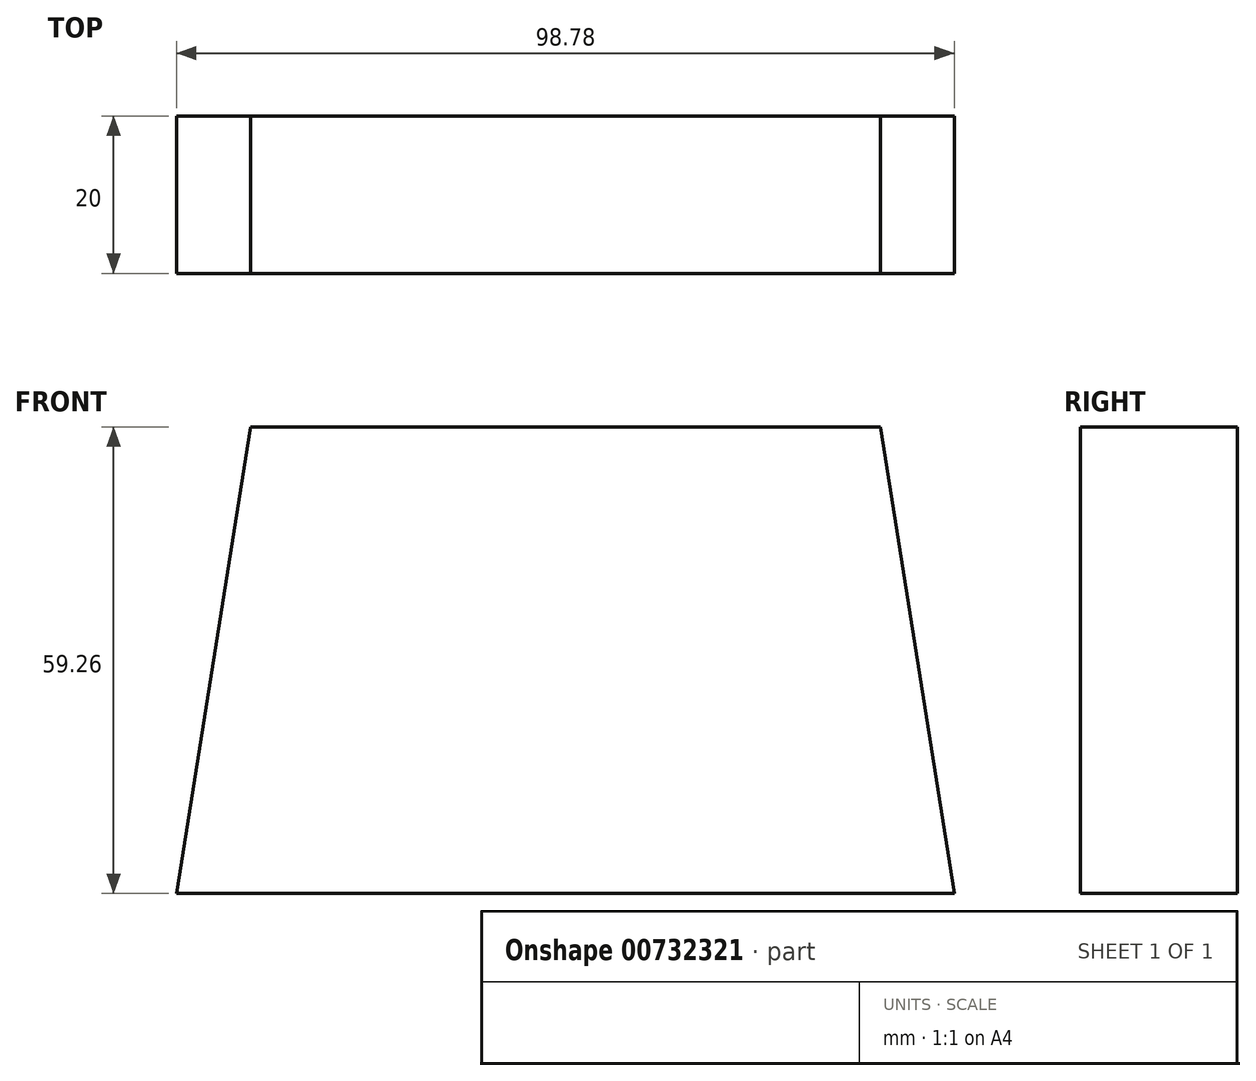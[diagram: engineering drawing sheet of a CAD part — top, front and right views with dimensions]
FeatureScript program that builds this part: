
annotation { "Feature Type Name" : "Feature", "Feature Type Description" : "" }
export const myFeature = defineFeature(function(context is Context, id is Id, definition is map)
    precondition{}
    {
        {
            var Q0;
            Q0=qCreatedBy(makeId("Front.planeOp"),FACE);
            var sketch = newSketch(context, id + "F0", { "sketchPlane" : qUnion([Q0])});
            skLineSegment(sketch, "E0", {"start": v(0, 0) * mm, "end": v(80, 0) * mm});
            skLineSegment(sketch, "E1", {"start": v(80, 0) * mm, "end": v(89.39, -59.26) * mm});
            skLineSegment(sketch, "E2", {"start": v(0, 0) * mm, "end": v(-9.39, -59.26) * mm});
            skLineSegment(sketch, "E3", {"start": v(-9.39, -59.26) * mm, "end": v(89.39, -59.26) * mm});
            skSolve(sketch);
        }
        {
            var Q0;
            Q0=makeQuery(id+"F0.imprint","IMPRINT",FACE,{"disambiguationData":[TD([[makeQuery(id+"F0.imprint","IMPRINT",EDGE,{"derivedFrom":sQuery(id+"F0.wireOp",EDGE,"E0")}),-1.0]])]});
            extrude(context, id + "F1", {"entities" : qUnion([Q0]), "depth" : 20 * mm, "offsetDistance" : 25 * mm});
        }
    });
